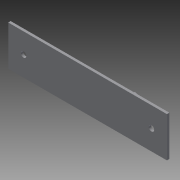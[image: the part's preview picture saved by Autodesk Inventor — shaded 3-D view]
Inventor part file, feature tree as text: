
AUTODESK INVENTOR PART (.ipt)
format: ipt  version: 2014 (Build 180170000, 170)  size: 2,155,008 bytes
history: native  units: mm
features: extrude x3, sketch x3
ambient origin geometry x8: Origin, YZ Plane, XZ Plane, XY Plane, X Axis, Y Axis, Z Axis, Center Point
bodies: Solid1 (feature_tree)
feature tree (6):
  extrude  "Extrusion1"  Depth=26.0mm
  extrude  "Extrusion2"  Depth=1.6mm TaperAngle=0.0deg
  extrude  "Extrusion3"  Depth=10.0mm
  sketch  "Sketch1"  dims[d0=103.0mm d1=26.0mm]
  sketch  "Sketch2"  dims[d2=1.6mm d3=0.0mm d4=1.6mm d5=0.0mm]
  sketch  "Sketch3"  dims[d6=3.6mm d7=3.6mm d8=10.0mm d9=10.0mm d10=3.6mm d11=0.0mm]
